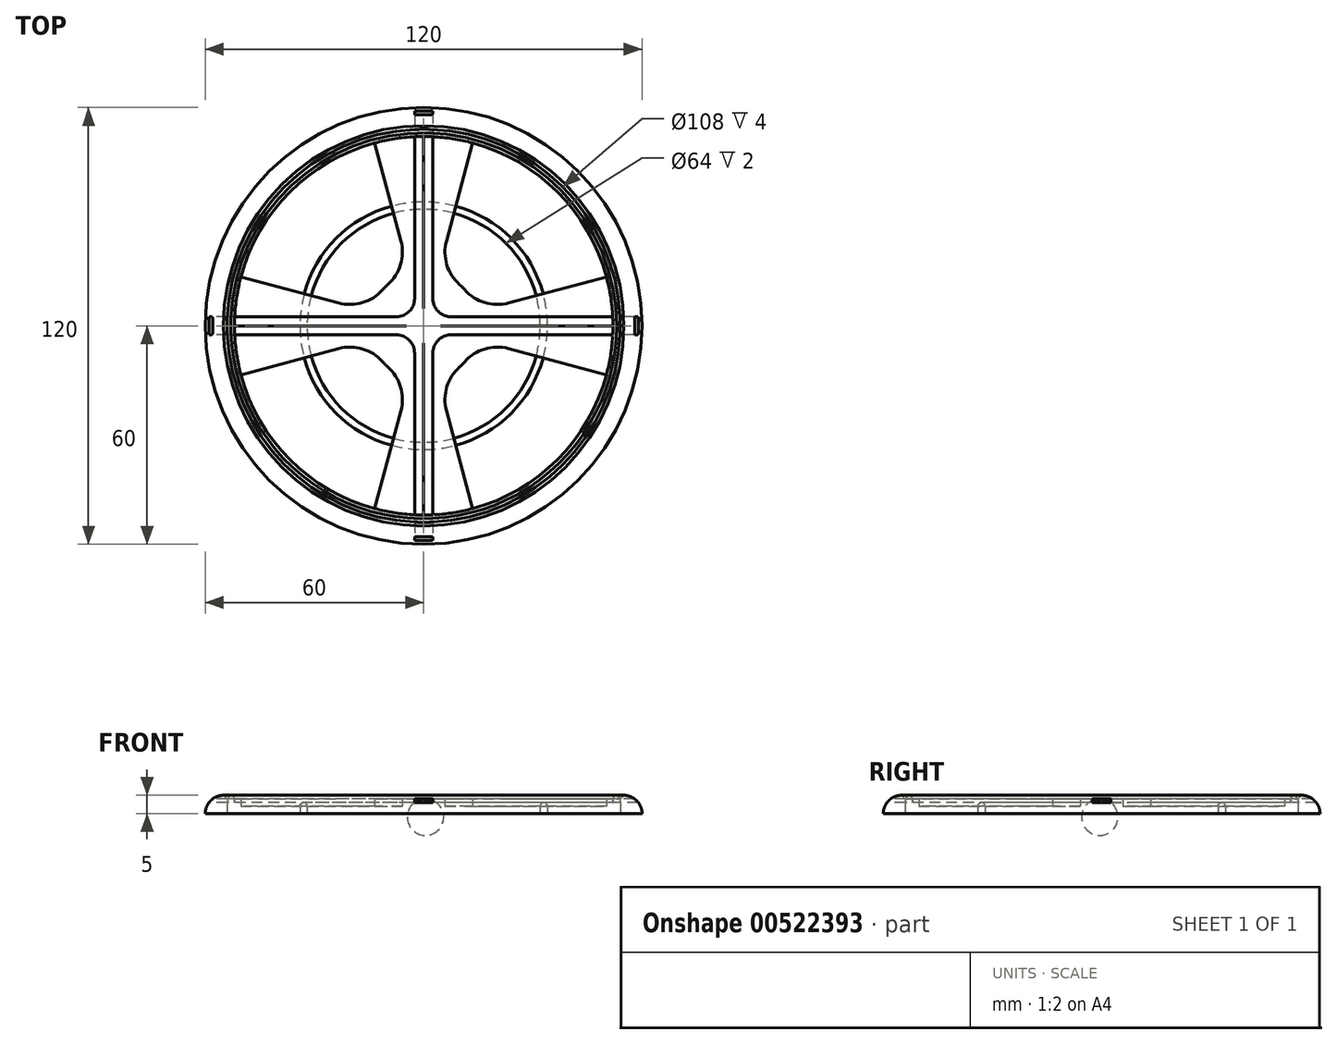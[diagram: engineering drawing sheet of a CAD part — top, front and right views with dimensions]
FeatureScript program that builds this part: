
annotation { "Feature Type Name" : "Feature", "Feature Type Description" : "" }
export const myFeature = defineFeature(function(context is Context, id is Id, definition is map)
    precondition{}
    {
        {
            var Q0;
            Q0=qCreatedBy(makeId("Top.planeOp"),FACE);
            var sketch = newSketch(context, id + "F0", { "sketchPlane" : qUnion([Q0])});
            skCircle(sketch, "E0", {"center": v(0, 0) * mm, "radius": 60 * mm});
            skSolve(sketch);
        }
        {
            var Q0;
            Q0=makeQuery(id+"F0.imprint","IMPRINT",FACE,{"disambiguationData":[TD([[makeQuery(id+"F0.imprint","IMPRINT",EDGE,{"derivedFrom":sQuery(id+"F0.wireOp",EDGE,"E0")}),1.0]])]});
            extrude(context, id + "F1", {"entities" : qUnion([Q0]), "depth" : 5 * mm, "offsetDistance" : 25 * mm});
        }
        {
            var Q0;
            Q0=makeQuery(id+"F1.opExtrude","CAP_FACE",FACE,{"disambiguationData":[OSD([sQuery(id+"F0.wireOp",EDGE,"E0")])],"isStart":false});
            var Q1;
            Q1=makeQuery(id+"F1.opExtrude","CAP_FACE",FACE,{"disambiguationData":[OSD([sQuery(id+"F0.wireOp",EDGE,"E0")])],"isStart":true});
            shell(context, id + "F2", {"entities" : qUnion([Q0, Q1]), "thickness" : 6 * mm});
        }
        {
            var Q0;
            Q0=makeQuery(id+"F1.opExtrude","CAP_EDGE",EDGE,{"disambiguationData":[OSD([sQuery(id+"F0.wireOp",EDGE,"E0")])],"isStart":false});
            fillet(context, id + "F3", {"entities" : qUnion([Q0]), "radius" : 5 * mm, "tangentPropagation" : true, "allowEdgeOverflow" : false});
        }
        {
            var Q0;
            {var subQ0=sQuery(id+"F0.wireOp",EDGE,"E0");Q0=makeQuery(id+"F2.opShell","OFFSET_EDGE",EDGE,{"disambiguationData":[OSD([subQ0]),TDD([makeQuery(id+"F1.opExtrude","CAP_EDGE",EDGE,{"disambiguationData":[OSD([subQ0])],"isStart":false})])]});}
            chamfer(context, id + "F4", {"entities" : qUnion([Q0]), "width" : 1 * mm, "tangentPropagation" : true});
        }
        {
            var Q0;
            Q0=qCreatedBy(makeId("Top.planeOp"),FACE);
            var sketch = newSketch(context, id + "F5", { "sketchPlane" : qUnion([Q0])});
            skCircle(sketch, "E1", {"center": v(0, 0) * mm, "radius": 54 * mm});
            skSolve(sketch);
        }
        {
            var Q0;
            Q0=makeQuery(id+"F5.imprint","IMPRINT",FACE,{"disambiguationData":[TD([[makeQuery(id+"F5.imprint","IMPRINT",EDGE,{"derivedFrom":sQuery(id+"F5.wireOp",EDGE,"E1")}),1.0]])]});
            extrude(context, id + "F6", {"entities" : qUnion([Q0]), "depth" : 5 * mm, "offsetDistance" : 25 * mm});
        }
        {
            var Q0;
            Q0=makeQuery(id+"F6.opExtrude","CAP_FACE",FACE,{"disambiguationData":[OSD([sQuery(id+"F5.wireOp",EDGE,"E1")])],"isStart":false});
            shell(context, id + "F7", {"entities" : qUnion([Q0]), "thickness" : 2 * mm});
        }
        {
            var Q0;
            Q0=makeQuery(id+"F6.opExtrude","CAP_EDGE",EDGE,{"disambiguationData":[OSD([sQuery(id+"F5.wireOp",EDGE,"E1")])],"isStart":false});
            chamfer(context, id + "F8", {"entities" : qUnion([Q0]), "width" : 1 * mm, "tangentPropagation" : true});
        }
        {
            var Q0;
            {var subQ0=sQuery(id+"F5.wireOp",EDGE,"E1");Q0=makeQuery(id+"F7.opShell","OFFSET_EDGE",EDGE,{"disambiguationData":[OSD([subQ0]),TDD([makeQuery(id+"F6.opExtrude","CAP_EDGE",EDGE,{"disambiguationData":[OSD([subQ0])],"isStart":false})])]});}
            fillet(context, id + "F9", {"entities" : qUnion([Q0]), "radius" : 1 * mm, "tangentPropagation" : true, "allowEdgeOverflow" : false});
        }
        {
            var Q0;
            Q0=qCreatedBy(makeId("Top.planeOp"),FACE);
            var sketch = newSketch(context, id + "F10", { "sketchPlane" : qUnion([Q0])});
            skLineSegment(sketch, "E2", {"start": v(-13.46, 50.23) * mm, "end": v(0, 0) * mm});
            skLineSegment(sketch, "E3", {"start": v(0, 0) * mm, "end": v(13.46, 50.23) * mm});
            skArc(sketch, "E4", {"start": v(13.46, 50.23) * mm, "mid": v(0, 52) * mm, "end": v(-13.46, 50.23) * mm});
            skSolve(sketch);
        }
        {
            var Q0;
            Q0 = qSketchRegion(id + "F10", true);
            extrude(context, id + "F11", {"entities" : qUnion([Q0]), "depth" : 4 * mm, "offsetDistance" : 25 * mm});
        }
        {
            var Q0;
            Q0=makeQuery(id+"F11.opExtrude","SWEPT_BODY",BODY,{"disambiguationData":[OSD([sQuery(id+"F10.wireOp",EDGE,"E2"),sQuery(id+"F10.wireOp",EDGE,"E3"),sQuery(id+"F10.wireOp",EDGE,"E4")])]});
            var Q1;
            Q1=makeQuery(id+"F11.opExtrude","SWEPT_EDGE",EDGE,{"disambiguationData":[OSD([sQuery(id+"F10.wireOp",EDGE,"E2"),sQuery(id+"F10.wireOp",EDGE,"E3")])]});
            circularPattern(context, id + "F12", {"entities" : qUnion([Q0]), "axis" : qUnion([Q1]), "angle" : 360 * degree, "instanceCount" : 4, "equalSpace" : true});
        }
        {
            var Q0;
            Q0=qCreatedBy(makeId("Top.planeOp"),FACE);
            var sketch = newSketch(context, id + "F13", { "sketchPlane" : qUnion([Q0])});
            skCircle(sketch, "E5", {"center": v(0, 0) * mm, "radius": 34 * mm});
            skCircle(sketch, "E6", {"center": v(0, 0) * mm, "radius": 32 * mm});
            skSolve(sketch);
        }
        {
            var Q0;
            Q0 = qSketchRegion(id + "F13", true);
            extrude(context, id + "F14", {"entities" : qUnion([Q0]), "depth" : 3 * mm, "offsetDistance" : 25 * mm});
        }
        {
            var Q0;
            Q0=makeQuery(id+"F14.opExtrude","CAP_FACE",FACE,{"disambiguationData":[OSD([sQuery(id+"F13.wireOp",EDGE,"E5"),sQuery(id+"F13.wireOp",EDGE,"E6")])],"isStart":false});
            fillet(context, id + "F15", {"entities" : qUnion([Q0]), "radius" : 1 * mm, "tangentPropagation" : true, "allowEdgeOverflow" : false});
        }
        {
            var Q0;
            Q0=qCreatedBy(makeId("Top.planeOp"),FACE);
            var sketch = newSketch(context, id + "F16", { "sketchPlane" : qUnion([Q0])});
            skCircle(sketch, "E7", {"center": v(0, 0) * mm, "radius": 15 * mm});
            skSolve(sketch);
        }
        {
            var Q0;
            Q0 = qSketchRegion(id + "F16", true);
            var Q1;
            Q1=sQuery(id+"F16.wireOp",EDGE,"E7");
            extrude(context, id + "F17", {"entities" : qUnion([Q0]), "operationType" : NewBodyOperationType.ADD, "surfaceEntities" : qUnion([Q1]), "depth" : 4 * mm, "offsetDistance" : 25 * mm});
        }
        {
            var Q0;
            Q0=makeQuery(id+"F17.boolean.opBoolean","INTERSECT",EDGE,{"derivedFrom":[makeQuery(id+"F12.opPattern","COPY",FACE,{"derivedFrom":makeQuery(id+"F11.opExtrude","SWEPT_FACE",FACE,{"disambiguationData":[OSD([sQuery(id+"F10.wireOp",EDGE,"E2")])]}),"instanceName":"3"}),makeQuery(id+"F17.opExtrude","SWEPT_FACE",FACE,{"disambiguationData":[OSD([sQuery(id+"F16.wireOp",EDGE,"E7")])]})]});
            var Q1;
            Q1=makeQuery(id+"F17.boolean.opBoolean","INTERSECT",EDGE,{"derivedFrom":[makeQuery(id+"F12.opPattern","COPY",FACE,{"derivedFrom":makeQuery(id+"F11.opExtrude","SWEPT_FACE",FACE,{"disambiguationData":[OSD([sQuery(id+"F10.wireOp",EDGE,"E3")])]}),"instanceName":"2"}),makeQuery(id+"F17.opExtrude","SWEPT_FACE",FACE,{"disambiguationData":[OSD([sQuery(id+"F16.wireOp",EDGE,"E7")])]})]});
            var Q2;
            Q2=makeQuery(id+"F17.boolean.opBoolean","INTERSECT",EDGE,{"derivedFrom":[makeQuery(id+"F12.opPattern","COPY",FACE,{"derivedFrom":makeQuery(id+"F11.opExtrude","SWEPT_FACE",FACE,{"disambiguationData":[OSD([sQuery(id+"F10.wireOp",EDGE,"E2")])]}),"instanceName":"2"}),makeQuery(id+"F17.opExtrude","SWEPT_FACE",FACE,{"disambiguationData":[OSD([sQuery(id+"F16.wireOp",EDGE,"E7")])]})]});
            var Q3;
            Q3=makeQuery(id+"F17.boolean.opBoolean","INTERSECT",EDGE,{"derivedFrom":[makeQuery(id+"F12.opPattern","COPY",FACE,{"derivedFrom":makeQuery(id+"F11.opExtrude","SWEPT_FACE",FACE,{"disambiguationData":[OSD([sQuery(id+"F10.wireOp",EDGE,"E3")])]}),"instanceName":"1"}),makeQuery(id+"F17.opExtrude","SWEPT_FACE",FACE,{"disambiguationData":[OSD([sQuery(id+"F16.wireOp",EDGE,"E7")])]})]});
            var Q4;
            Q4=makeQuery(id+"F17.boolean.opBoolean","INTERSECT",EDGE,{"derivedFrom":[makeQuery(id+"F12.opPattern","COPY",FACE,{"derivedFrom":makeQuery(id+"F11.opExtrude","SWEPT_FACE",FACE,{"disambiguationData":[OSD([sQuery(id+"F10.wireOp",EDGE,"E2")])]}),"instanceName":"1"}),makeQuery(id+"F17.opExtrude","SWEPT_FACE",FACE,{"disambiguationData":[OSD([sQuery(id+"F16.wireOp",EDGE,"E7")])]})]});
            var Q5;
            Q5=makeQuery(id+"F17.boolean.opBoolean","INTERSECT",EDGE,{"derivedFrom":[makeQuery(id+"F11.opExtrude","SWEPT_FACE",FACE,{"disambiguationData":[OSD([sQuery(id+"F10.wireOp",EDGE,"E3")])]}),makeQuery(id+"F17.opExtrude","SWEPT_FACE",FACE,{"disambiguationData":[OSD([sQuery(id+"F16.wireOp",EDGE,"E7")])]})]});
            var Q6;
            Q6=makeQuery(id+"F17.boolean.opBoolean","INTERSECT",EDGE,{"derivedFrom":[makeQuery(id+"F11.opExtrude","SWEPT_FACE",FACE,{"disambiguationData":[OSD([sQuery(id+"F10.wireOp",EDGE,"E2")])]}),makeQuery(id+"F17.opExtrude","SWEPT_FACE",FACE,{"disambiguationData":[OSD([sQuery(id+"F16.wireOp",EDGE,"E7")])]})]});
            var Q7;
            Q7=makeQuery(id+"F17.boolean.opBoolean","INTERSECT",EDGE,{"derivedFrom":[makeQuery(id+"F12.opPattern","COPY",FACE,{"derivedFrom":makeQuery(id+"F11.opExtrude","SWEPT_FACE",FACE,{"disambiguationData":[OSD([sQuery(id+"F10.wireOp",EDGE,"E3")])]}),"instanceName":"3"}),makeQuery(id+"F17.opExtrude","SWEPT_FACE",FACE,{"disambiguationData":[OSD([sQuery(id+"F16.wireOp",EDGE,"E7")])]})]});
            fillet(context, id + "F18", {"entities" : qUnion([Q0, Q1, Q2, Q3, Q4, Q5, Q6, Q7]), "radius" : 12 * mm, "tangentPropagation" : true, "allowEdgeOverflow" : false});
        }
        {
            var Q0;
            {var subQ0=makeQuery(id+"F11.opExtrude","CAP_FACE",FACE,{"disambiguationData":[OSD([sQuery(id+"F10.wireOp",EDGE,"E2"),sQuery(id+"F10.wireOp",EDGE,"E3"),sQuery(id+"F10.wireOp",EDGE,"E4")])],"isStart":false});Q0=makeQuery(id+"F17.boolean.opBoolean","MERGE",FACE,{"derivedFrom":[subQ0,makeQuery(id+"F12.opPattern","COPY",FACE,{"derivedFrom":subQ0,"instanceName":"1"}),makeQuery(id+"F12.opPattern","COPY",FACE,{"derivedFrom":subQ0,"instanceName":"2"}),makeQuery(id+"F12.opPattern","COPY",FACE,{"derivedFrom":subQ0,"instanceName":"3"}),makeQuery(id+"F17.opExtrude","CAP_FACE",FACE,{"disambiguationData":[OSD([sQuery(id+"F16.wireOp",EDGE,"E7")])],"isStart":false})]});}
            var sketch = newSketch(context, id + "F19", { "sketchPlane" : qUnion([Q0])});
            skLineSegment(sketch, "E8.bottom", {"start": v(-2.5, 66.65) * mm, "end": v(2.5, 66.65) * mm});
            skLineSegment(sketch, "E8.top", {"start": v(-2.5, -65.74) * mm, "end": v(2.5, -65.74) * mm});
            skLineSegment(sketch, "E8.left", {"start": v(-2.5, 66.65) * mm, "end": v(-2.5, 2.5) * mm});
            skLineSegment(sketch, "E8.right", {"start": v(2.5, 66.65) * mm, "end": v(2.5, 2.5) * mm});
            skLineSegment(sketch, "E9.bottom", {"start": v(66.92, 2.5) * mm, "end": v(2.5, 2.5) * mm});
            skLineSegment(sketch, "E9.top", {"start": v(66.92, -2.5) * mm, "end": v(2.5, -2.5) * mm});
            skLineSegment(sketch, "E9.left", {"start": v(66.92, 2.5) * mm, "end": v(66.92, -2.5) * mm});
            skLineSegment(sketch, "E9.right", {"start": v(-62.38, 2.5) * mm, "end": v(-62.38, -2.5) * mm});
            skLineSegment(sketch, "E10.trimOffspring", {"start": v(-2.5, -2.5) * mm, "end": v(-2.5, -65.74) * mm});
            skLineSegment(sketch, "E11.trimOffspring", {"start": v(-2.5, 2.5) * mm, "end": v(-62.38, 2.5) * mm});
            skLineSegment(sketch, "E12.trimOffspring", {"start": v(2.5, -2.5) * mm, "end": v(2.5, -65.74) * mm});
            skLineSegment(sketch, "E13.trimOffspring", {"start": v(-2.5, -2.5) * mm, "end": v(-62.38, -2.5) * mm});
            skSolve(sketch);
        }
        {
            var Q0;
            Q0 = qSketchRegion(id + "F19", true);
            extrude(context, id + "F20", {"entities" : qUnion([Q0]), "operationType" : NewBodyOperationType.REMOVE, "oppositeDirection" : true, "depth" : 1 * mm, "offsetDistance" : 25 * mm});
        }
        {
            var Q0;
            Q0=makeQuery(id+"F20.boolean.opBoolean","COPY",EDGE,{"derivedFrom":makeQuery(id+"F20.opExtrude","SWEPT_EDGE",EDGE,{"disambiguationData":[OSD([sQuery(id+"F19.wireOp",EDGE,"E8.left"),sQuery(id+"F19.wireOp",EDGE,"E11.trimOffspring")])]})});
            var Q1;
            Q1=makeQuery(id+"F20.boolean.opBoolean","COPY",EDGE,{"derivedFrom":makeQuery(id+"F20.opExtrude","SWEPT_EDGE",EDGE,{"disambiguationData":[OSD([sQuery(id+"F19.wireOp",EDGE,"E10.trimOffspring"),sQuery(id+"F19.wireOp",EDGE,"E13.trimOffspring")])]})});
            var Q2;
            Q2=makeQuery(id+"F20.boolean.opBoolean","COPY",EDGE,{"derivedFrom":makeQuery(id+"F20.opExtrude","SWEPT_EDGE",EDGE,{"disambiguationData":[OSD([sQuery(id+"F19.wireOp",EDGE,"E9.top"),sQuery(id+"F19.wireOp",EDGE,"E12.trimOffspring")])]})});
            var Q3;
            Q3=makeQuery(id+"F20.boolean.opBoolean","COPY",EDGE,{"derivedFrom":makeQuery(id+"F20.opExtrude","SWEPT_EDGE",EDGE,{"disambiguationData":[OSD([sQuery(id+"F19.wireOp",EDGE,"E8.right"),sQuery(id+"F19.wireOp",EDGE,"E9.bottom")])]})});
            fillet(context, id + "F21", {"entities" : qUnion([Q0, Q1, Q2, Q3]), "radius" : 5 * mm, "tangentPropagation" : true, "allowEdgeOverflow" : false});
        }
        {
            var Q0;
            Q0=makeQuery(id+"F20.boolean.opBoolean","COPY",EDGE,{"derivedFrom":makeQuery(id+"F20.opExtrude","CAP_EDGE",EDGE,{"disambiguationData":[OSD([sQuery(id+"F19.wireOp",EDGE,"E13.trimOffspring")])],"isStart":true})});
            var Q1;
            Q1=makeQuery(id+"F20.boolean.opBoolean","COPY",EDGE,{"derivedFrom":makeQuery(id+"F20.opExtrude","CAP_EDGE",EDGE,{"disambiguationData":[OSD([sQuery(id+"F19.wireOp",EDGE,"E8.right")])],"isStart":true})});
            var Q2;
            {var subQ0=sQuery(id+"F10.wireOp",EDGE,"E2");var subQ2=sQuery(id+"F19.wireOp",EDGE,"E12.trimOffspring");var subQ3=sQuery(id+"F10.wireOp",EDGE,"E4");var subQ5=sQuery(id+"F10.wireOp",EDGE,"E3");var subQ6=makeQuery(id+"F12.opPattern","COPY",FACE,{"derivedFrom":makeQuery(id+"F11.opExtrude","SWEPT_FACE",FACE,{"disambiguationData":[OSD([subQ5])]}),"instanceName":"1"});var subQ7=sQuery(id+"F16.wireOp",EDGE,"E7");var subQ9=sQuery(id+"F19.wireOp",EDGE,"E9.top");var subQ10=makeQuery(id+"F11.opExtrude","CAP_FACE",FACE,{"disambiguationData":[OSD([subQ0,subQ5,subQ3])],"isStart":false});Q2=makeQuery(id+"F21.opFillet","BLEND_EDGE",EDGE,{"blendedFrom":[makeQuery(id+"F20.boolean.opBoolean","COPY",EDGE,{"derivedFrom":makeQuery(id+"F20.opExtrude","SWEPT_EDGE",EDGE,{"disambiguationData":[OSD([subQ9,subQ2])]})}),makeQuery(id+"F20.boolean.opBoolean","SPLIT",FACE,{"disambiguationData":[TD([subQ6])],"derivedFrom":makeQuery(id+"F17.boolean.opBoolean","MERGE",FACE,{"derivedFrom":[subQ10,makeQuery(id+"F12.opPattern","COPY",FACE,{"derivedFrom":subQ10,"instanceName":"1"}),makeQuery(id+"F12.opPattern","COPY",FACE,{"derivedFrom":subQ10,"instanceName":"2"}),makeQuery(id+"F12.opPattern","COPY",FACE,{"derivedFrom":subQ10,"instanceName":"3"}),makeQuery(id+"F17.opExtrude","CAP_FACE",FACE,{"disambiguationData":[OSD([subQ7])],"isStart":false})]})})],"blendedInto":[makeQuery(id+"F20.boolean.opBoolean","SPLIT",FACE,{"disambiguationData":[TD([subQ6])],"derivedFrom":makeQuery(id+"F17.boolean.opBoolean","MERGE",FACE,{"derivedFrom":[subQ10,makeQuery(id+"F12.opPattern","COPY",FACE,{"derivedFrom":subQ10,"instanceName":"1"}),makeQuery(id+"F12.opPattern","COPY",FACE,{"derivedFrom":subQ10,"instanceName":"2"}),makeQuery(id+"F12.opPattern","COPY",FACE,{"derivedFrom":subQ10,"instanceName":"3"}),makeQuery(id+"F17.opExtrude","CAP_FACE",FACE,{"disambiguationData":[OSD([subQ7])],"isStart":false})]})})]});}
            var Q3;
            Q3=makeQuery(id+"F20.boolean.opBoolean","COPY",EDGE,{"derivedFrom":makeQuery(id+"F20.opExtrude","CAP_EDGE",EDGE,{"disambiguationData":[OSD([sQuery(id+"F19.wireOp",EDGE,"E11.trimOffspring")])],"isStart":true})});
            fillet(context, id + "F22", {"entities" : qUnion([Q0, Q1, Q2, Q3]), "radius" : 0.5 * mm, "tangentPropagation" : true, "allowEdgeOverflow" : false});
        }
        {
            var Q0;
            Q0=makeQuery(id+"F20.boolean.opBoolean","COPY",FACE,{"derivedFrom":makeQuery(id+"F20.opExtrude","CAP_FACE",FACE,{"disambiguationData":[OSD([sQuery(id+"F19.wireOp",EDGE,"E8.bottom"),sQuery(id+"F19.wireOp",EDGE,"E8.top"),sQuery(id+"F19.wireOp",EDGE,"E8.left"),sQuery(id+"F19.wireOp",EDGE,"E8.right"),sQuery(id+"F19.wireOp",EDGE,"E9.bottom"),sQuery(id+"F19.wireOp",EDGE,"E9.top"),sQuery(id+"F19.wireOp",EDGE,"E9.left"),sQuery(id+"F19.wireOp",EDGE,"E9.right"),sQuery(id+"F19.wireOp",EDGE,"E10.trimOffspring"),sQuery(id+"F19.wireOp",EDGE,"E11.trimOffspring"),sQuery(id+"F19.wireOp",EDGE,"E12.trimOffspring"),sQuery(id+"F19.wireOp",EDGE,"E13.trimOffspring")])],"isStart":false})});
            var sketch = newSketch(context, id + "F23", { "sketchPlane" : qUnion([Q0])});
            skLineSegment(sketch, "E14.left", {"start": v(-2.5, 51.94) * mm, "end": v(-2.5, 2.5) * mm});
            skLineSegment(sketch, "E14.right", {"start": v(2.5, 51.94) * mm, "end": v(2.5, 2.5) * mm});
            skLineSegment(sketch, "E15.bottom", {"start": v(51.94, 2.5) * mm, "end": v(2.5, 2.5) * mm});
            skLineSegment(sketch, "E15.top", {"start": v(51.94, -2.5) * mm, "end": v(2.5, -2.5) * mm});
            skArc(sketch, "E16", {"start": v(-51.94, 2.5) * mm, "mid": v(-52, 0) * mm, "end": v(-51.94, -2.5) * mm});
            skLineSegment(sketch, "E17.trimOffspring", {"start": v(-2.5, -2.5) * mm, "end": v(-2.5, -51.94) * mm});
            skLineSegment(sketch, "E18.trimOffspring", {"start": v(-2.5, 2.5) * mm, "end": v(-51.94, 2.5) * mm});
            skLineSegment(sketch, "E19.trimOffspring", {"start": v(2.5, -2.5) * mm, "end": v(2.5, -51.94) * mm});
            skLineSegment(sketch, "E20.trimOffspring", {"start": v(-2.5, -2.5) * mm, "end": v(-51.94, -2.5) * mm});
            skArc(sketch, "E21.trimOffspring", {"start": v(-2.5, -51.94) * mm, "mid": v(0, -52) * mm, "end": v(2.5, -51.94) * mm});
            skArc(sketch, "E22.trimOffspring", {"start": v(51.94, -2.5) * mm, "mid": v(52, 0) * mm, "end": v(51.94, 2.5) * mm});
            skArc(sketch, "E23.trimOffspring", {"start": v(2.5, 51.94) * mm, "mid": v(0, 52) * mm, "end": v(-2.5, 51.94) * mm});
            skSolve(sketch);
        }
        {
            var Q0;
            Q0 = qSketchRegion(id + "F23", true);
            extrude(context, id + "F24", {"entities" : qUnion([Q0]), "depth" : 1 * mm, "offsetDistance" : 25 * mm});
        }
        {
            var Q0;
            Q0=makeQuery(id+"F24.opExtrude","SWEPT_EDGE",EDGE,{"disambiguationData":[OSD([sQuery(id+"F23.wireOp",EDGE,"E15.top"),sQuery(id+"F23.wireOp",EDGE,"E19.trimOffspring")])]});
            var Q1;
            Q1=makeQuery(id+"F24.opExtrude","SWEPT_EDGE",EDGE,{"disambiguationData":[OSD([sQuery(id+"F23.wireOp",EDGE,"E14.right"),sQuery(id+"F23.wireOp",EDGE,"E15.bottom")])]});
            var Q2;
            Q2=makeQuery(id+"F24.opExtrude","SWEPT_EDGE",EDGE,{"disambiguationData":[OSD([sQuery(id+"F23.wireOp",EDGE,"E14.left"),sQuery(id+"F23.wireOp",EDGE,"E18.trimOffspring")])]});
            var Q3;
            Q3=makeQuery(id+"F24.opExtrude","SWEPT_EDGE",EDGE,{"disambiguationData":[OSD([sQuery(id+"F23.wireOp",EDGE,"E17.trimOffspring"),sQuery(id+"F23.wireOp",EDGE,"E20.trimOffspring")])]});
            fillet(context, id + "F25", {"entities" : qUnion([Q0, Q1, Q2, Q3]), "radius" : 5 * mm, "tangentPropagation" : true, "allowEdgeOverflow" : false});
        }
        {
            var Q0;
            Q0=makeQuery(id+"F24.opExtrude","CAP_EDGE",EDGE,{"disambiguationData":[OSD([sQuery(id+"F23.wireOp",EDGE,"E18.trimOffspring")])],"isStart":false});
            var Q1;
            Q1=makeQuery(id+"F24.opExtrude","CAP_EDGE",EDGE,{"disambiguationData":[OSD([sQuery(id+"F23.wireOp",EDGE,"E20.trimOffspring")])],"isStart":false});
            var Q2;
            Q2=makeQuery(id+"F24.opExtrude","CAP_EDGE",EDGE,{"disambiguationData":[OSD([sQuery(id+"F23.wireOp",EDGE,"E19.trimOffspring")])],"isStart":false});
            var Q3;
            Q3=makeQuery(id+"F24.opExtrude","CAP_EDGE",EDGE,{"disambiguationData":[OSD([sQuery(id+"F23.wireOp",EDGE,"E15.bottom")])],"isStart":false});
            fillet(context, id + "F26", {"entities" : qUnion([Q0, Q1, Q2, Q3]), "radius" : 5 * mm, "tangentPropagation" : true, "allowEdgeOverflow" : false});
        }
    });
